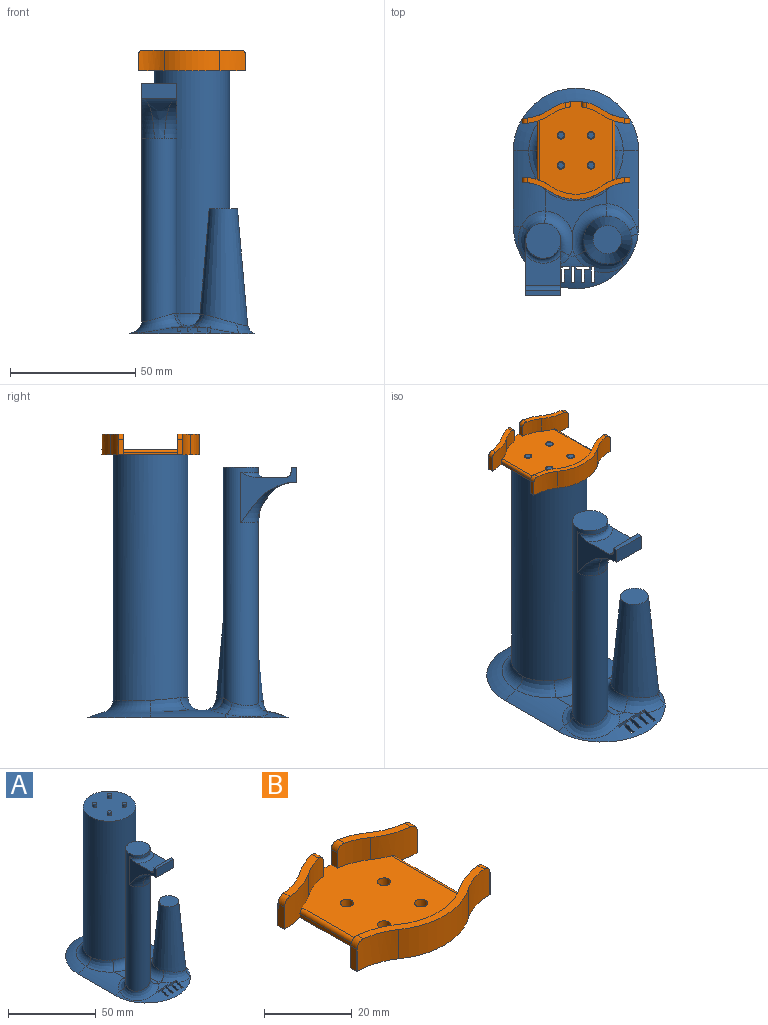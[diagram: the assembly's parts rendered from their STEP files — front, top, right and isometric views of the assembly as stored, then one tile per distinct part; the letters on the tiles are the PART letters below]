
ASSEMBLY  parts=2 mates=1
PART A: 71 faces, bbox 75.8x97.1x107.7 mm
  f0: plane 0.12x0.04mm, normal (0,0,-1), area 0mm2, adj f52,f53,f60
  f1: plane 14x14mm, normal (0,0,1), area 153.9mm2, adj f3
  f2: plane 14x2mm, normal (0,0,1), area 28mm2, adj f52,f53,f54,f56
  f3: cylinder r=7mm len=93.92mm, axis (0,0,-1), area 3634.1mm2, adj f1,f44,f45,f48,f52,f54,f58,f59
  f4: torus R=12.11mm, axis (0,0,-1), area 1.8mm2, adj f31,f38,f46
  f5: plane 24.21x16.62mm, normal (0,0,1), area 156mm2, adj f37,f38,f40,f48,f51
  f6: plane 2.56x2.06mm, normal (0,1,0), area 4.9mm2, adj f7,f29,f31,f39
  f7: plane 5.19x2.42mm, normal (-1,0,0), area 9.1mm2, adj f6,f8,f31,f39
  f8: plane 1.32x0.94mm, normal (0,1,0), area 1.1mm2, adj f7,f9,f31,f39
  f9: plane 5.19x2.34mm, normal (1,0,0), area 8.6mm2, adj f8,f10,f31,f39
  f10: plane 2.4x2.06mm, normal (0,1,0), area 4.5mm2, adj f9,f11,f31,f39
  f11: plane 2.39x1.01mm, normal (1,0,0), area 2.3mm2, adj f10,f12,f31,f39
  f12: plane 5.29x2.67mm, normal (0,-1,0), area 13.5mm2, adj f11,f29,f31,f39
  f13: plane 1.32x1.12mm, normal (0,1,0), area 1.4mm2, adj f14,f26,f31,f39
  f14: plane 6.19x2.68mm, normal (1,0,0), area 12.3mm2, adj f13,f15,f31,f39
  f15: plane 2.72x1.32mm, normal (0,-1,0), area 3.5mm2, adj f14,f26,f31,f39
  f16: plane 2.54x2.06mm, normal (0,1,0), area 4.9mm2, adj f17,f27,f31,f39
  f17: plane 5.19x2.48mm, normal (-1,0,0), area 9.5mm2, adj f16,f18,f31,f39
  f18: plane 1.32x1.08mm, normal (0,1,0), area 1.3mm2, adj f17,f19,f31,f39
  f19: plane 5.26x2.59mm, normal (1,0,0), area 9.7mm2, adj f18,f20,f31,f39
  f20: plane 2.6x2.06mm, normal (0,1,0), area 5.1mm2, adj f19,f21,f31,f39
  f21: plane 2.7x1mm, normal (1,0,0), area 2.6mm2, adj f20,f22,f31,f39
  f22: plane 5.34x2.74mm, normal (0,-1,0), area 14.1mm2, adj f21,f27,f31,f39,f50
  f23: plane 1.32x0.8mm, normal (0,1,0), area 0.9mm2, adj f24,f28,f31,f39
  f24: plane 6.23x2.71mm, normal (1,0,0), area 11mm2, adj f23,f25,f31,f39,f50
  f25: plane 2.78x1.32mm, normal (0,-1,0), area 3.5mm2, adj f24,f28,f31,f50
  f26: plane 6.22x2.73mm, normal (-1,0,0), area 12.5mm2, adj f13,f15,f31,f39
  f27: plane 2.66x1.02mm, normal (-1,0,0), area 2.5mm2, adj f16,f22,f31,f39,f50
  f28: plane 6.26x2.83mm, normal (-1,0,0), area 10.3mm2, adj f23,f25,f31,f39,f50
  f29: plane 2.67x1mm, normal (-1,0,0), area 2.6mm2, adj f6,f12,f31,f39
  f30: plane 3.1x2.31mm, normal (0,0,1), area 3.1mm2, adj f39,f48,f51
  f31: plane 80.03x50.03mm, normal (0,0,-1), area 3423.5mm2, adj f4,f6,f7,f8,f9,f10,f11,f12
  f32: cone r=10mm half-angle=5deg, axis (0,0,-1), area 2093.8mm2, adj f33,f46,f47,f49,f50,f51
  f33: plane 11.25x11.25mm, normal (0,0,1), area 99.4mm2, adj f32
  f34: cylinder r=15mm len=97.92mm, axis (0,0,-1), area 9198.3mm2, adj f35,f40,f41,f42,f43
  f35: plane 30x30mm, normal (0,0,1), area 687.2mm2, adj f34,f63,f65,f67,f69
  f36: torus R=12.11mm, axis (0,0,-1), area 452.2mm2, adj f31,f37,f38,f43
  f37: cylinder r=29.21mm len=30mm, axis (0,1,0), area 295.9mm2, adj f5,f31,f36,f39,f42,f45
  f38: cylinder r=29.21mm len=30mm, axis (0,1,0), area 247.3mm2, adj f4,f5,f31,f36,f41,f49
  f39: torus R=12.11mm, axis (0,0,-1), area 233.6mm2, adj f6,f7,f8,f9,f10,f11,f12,f13
  f40: torus R=20mm, axis (0,0,1), area 171.7mm2, adj f5,f34,f41,f42
  f41: bspline ~18.77x10.38mm, area 108.9mm2, adj f34,f38,f40,f43
  f42: bspline ~20.28x12.34mm, area 108.9mm2, adj f34,f37,f40,f43
  f43: torus R=20mm, axis (0,0,1), area 343.9mm2, adj f34,f36,f41,f42
  f44: bspline ~20.85x18.89mm, area 173mm2, adj f3,f39,f45,f48
  f45: bspline ~12.73x9.87mm, area 67.8mm2, adj f3,f37,f44,f48
  f46: bspline ~6.9x5.13mm, area 15mm2, adj f4,f32,f47,f49
  f47: bspline ~14.92x7.71mm, area 52mm2, adj f31,f32,f46,f50
  f48: torus R=12mm, axis (0,0,1), area 138.8mm2, adj f3,f5,f30,f44,f45,f51
  f49: bspline ~15.27x12.51mm, area 87.3mm2, adj f32,f38,f46,f51
  f50: bspline ~20.55x9.05mm, area 113.9mm2, adj f22,f24,f25,f27,f28,f32,f39,f47
  f51: torus R=14.32mm, axis (0,0,1), area 168.7mm2, adj f5,f30,f32,f48,f49,f50
  f52: plane 22.58x22.53mm, normal (-1,0,0), area 167.8mm2, adj f0,f2,f3,f53,f56,f57,f60,f61
  f53: plane 14.09x6.09mm, normal (0,-1,0), area 84mm2, adj f0,f2,f52,f54,f55,f59
  f54: plane 22.58x22.53mm, normal (1,0,0), area 167.8mm2, adj f2,f3,f53,f55,f56,f57,f58,f61
  f55: plane 0.12x0.04mm, normal (0,0,-1), area 0mm2, adj f53,f54,f58
  f56: plane 14x2mm, normal (0,1,0), area 28mm2, adj f2,f52,f54,f62
  f57: plane 14x12.34mm, normal (0,0,1), area 140.2mm2, adj f52,f54,f61,f62
  f58: torus R=23.05mm, axis (0,0,1), area 102.5mm2, adj f3,f54,f55,f59
  f59: bspline ~16.44x15.84mm, area 186.4mm2, adj f3,f53,f58,f60
  f60: torus R=23.05mm, axis (0,0,1), area 102.5mm2, adj f0,f3,f52,f59
  f61: torus R=9mm, axis (0,0,1), area 59mm2, adj f3,f52,f54,f57
  f62: cylinder r=2mm len=14mm, axis (1,0,0), area 44mm2, adj f52,f54,f56,f57
  f63: cylinder r=1.25mm len=2.5mm, axis (0,0,-1), area 15.7mm2, adj f35,f64
  f64: plane 2.5x2.5mm, normal (0,0,1), area 4.9mm2, adj f63
  f65: cylinder r=1.25mm len=2.5mm, axis (0,0,-1), area 15.7mm2, adj f35,f66
  f66: plane 2.5x2.5mm, normal (0,0,1), area 4.9mm2, adj f65
  f67: cylinder r=1.25mm len=2.5mm, axis (0,0,-1), area 15.7mm2, adj f35,f68
  f68: plane 2.5x2.5mm, normal (0,0,1), area 4.9mm2, adj f67
  f69: cylinder r=1.25mm len=2.5mm, axis (0,0,-1), area 15.7mm2, adj f35,f70
  f70: plane 2.5x2.5mm, normal (0,0,1), area 4.9mm2, adj f69
PART B: 46 faces, bbox 43x39x8.2 mm
  f0: plane 15.25x8.18mm, normal (0,0,1), area 33.2mm2, adj f2,f4,f5,f9,f39,f42
  f1: cylinder r=17.5mm len=7.77mm, axis (0,0,-1), area 51.3mm2, adj f3,f14,f35,f37,f38
  f2: cylinder r=19.5mm len=22.32mm, axis (0,0,-1), area 165.2mm2, adj f0,f9,f10,f14,f15,f35,f36,f37
  f3: cylinder r=20mm len=11.45mm, axis (0,0,-1), area 87.1mm2, adj f1,f13,f14,f15,f30,f35,f43,f44
  f4: cylinder r=17.5mm len=7.77mm, axis (0,0,-1), area 51.3mm2, adj f0,f5,f35,f36,f39
  f5: cylinder r=20mm len=11.45mm, axis (0,0,-1), area 87.1mm2, adj f0,f4,f6,f15,f29,f35,f42,f45
  f6: plane 6.58x0.04mm, normal (0,-1,0), area 0.2mm2, adj f5,f7,f15,f42
  f7: plane 6.2x2mm, normal (1,0,0), area 12.4mm2, adj f6,f8,f15,f42
  f8: plane 6.58x0.04mm, normal (0,1,0), area 0.2mm2, adj f7,f9,f15,f42
  f9: cylinder r=18mm len=10.3mm, axis (0,0,-1), area 89.1mm2, adj f0,f2,f8,f15,f42
  f10: cylinder r=18mm len=10.3mm, axis (0,0,-1), area 89.1mm2, adj f2,f11,f14,f15,f43
  f11: plane 6.58x0.04mm, normal (0,1,0), area 0.2mm2, adj f10,f12,f15,f43
  f12: plane 6.2x2mm, normal (-1,0,0), area 12.4mm2, adj f11,f13,f15,f43
  f13: plane 6.58x0.04mm, normal (0,-1,0), area 0.2mm2, adj f3,f12,f15,f43
  f14: plane 15.25x8.18mm, normal (0,0,1), area 33.2mm2, adj f1,f2,f3,f10,f38,f43
  f15: plane 43x39mm, normal (0,0,-1), area 1097mm2, adj f2,f3,f5,f6,f7,f8,f9,f10
  f16: cylinder r=20mm len=11.45mm, axis (0,0,-1), area 87.1mm2, adj f15,f17,f27,f28,f30,f35,f41,f44
  f17: plane 6.58x0.04mm, normal (0,1,0), area 0.2mm2, adj f15,f16,f18,f41
  f18: plane 6.2x2mm, normal (-1,0,0), area 12.4mm2, adj f15,f17,f19,f41
  f19: plane 6.58x0.04mm, normal (0,-1,0), area 0.2mm2, adj f15,f18,f20,f41
  f20: cylinder r=18mm len=10.3mm, axis (0,0,-1), area 89.1mm2, adj f15,f19,f21,f28,f41
  f21: cylinder r=19.5mm len=22.32mm, axis (0,0,-1), area 194.9mm2, adj f15,f20,f22,f28
  f22: cylinder r=18mm len=10.3mm, axis (0,0,-1), area 89.1mm2, adj f15,f21,f23,f28,f40
  f23: plane 6.58x0.04mm, normal (0,-1,0), area 0.2mm2, adj f15,f22,f24,f40
  f24: plane 6.2x2mm, normal (1,0,0), area 12.4mm2, adj f15,f23,f25,f40
  f25: plane 6.58x0.04mm, normal (0,1,0), area 0.2mm2, adj f15,f24,f26,f40
  f26: cylinder r=20mm len=11.45mm, axis (0,0,-1), area 87.1mm2, adj f15,f25,f27,f28,f29,f35,f40,f45
  f27: cylinder r=17.5mm len=20.03mm, axis (0,0,-1), area 132.2mm2, adj f16,f26,f28,f35
  f28: plane 39x8.65mm, normal (0,0,1), area 83.5mm2, adj f16,f20,f21,f22,f26,f27,f40,f41
  f29: plane 23.32x1mm, normal (1,0,0), area 23.3mm2, adj f5,f15,f26,f45
  f30: plane 23.32x1mm, normal (-1,0,0), area 23.3mm2, adj f3,f15,f16,f44
  f31: cylinder r=1.5mm len=3mm, axis (0,0,-1), area 18.8mm2, adj f15,f35
  f32: cylinder r=1.5mm len=3mm, axis (0,0,-1), area 18.8mm2, adj f15,f35
  f33: cylinder r=1.5mm len=3mm, axis (0,0,-1), area 18.8mm2, adj f15,f35
  f34: cylinder r=1.5mm len=3mm, axis (0,0,-1), area 18.8mm2, adj f15,f35
  f35: plane 37x29mm, normal (0,0,1), area 875.6mm2, adj f1,f2,f3,f4,f5,f16,f26,f27
  f36: plane 4.2x2.02mm, normal (-1,0,0), area 8.5mm2, adj f2,f4,f35,f39
  f37: plane 4.2x2.02mm, normal (1,0,0), area 8.5mm2, adj f1,f2,f35,f38
  f38: cylinder r=2mm len=2.39mm, axis (0,1,0), area 6.4mm2, adj f1,f2,f14,f37
  f39: cylinder r=2mm len=2.39mm, axis (0,-1,0), area 6.4mm2, adj f0,f2,f4,f36
  f40: cylinder r=2mm len=2.11mm, axis (0,-1,0), area 6.3mm2, adj f22,f23,f24,f25,f26,f28
  f41: cylinder r=2mm len=2.11mm, axis (0,1,0), area 6.3mm2, adj f16,f17,f18,f19,f20,f28
  f42: cylinder r=2mm len=2.11mm, axis (0,-1,0), area 6.3mm2, adj f0,f5,f6,f7,f8,f9
  f43: cylinder r=2mm len=2.11mm, axis (0,1,0), area 6.3mm2, adj f3,f10,f11,f12,f13,f14
  f44: cylinder r=1mm len=24mm, axis (0,1,0), area 37mm2, adj f3,f16,f30,f35
  f45: cylinder r=1mm len=24mm, axis (0,-1,0), area 37mm2, adj f5,f26,f29,f35
PLACE A t=(-9.87,16.69,-18.54)mm
PLACE B t=(-9.87,31.69,86.46)mm
MATE fastened B.f21 <-> A.f34  axis (0,0,-1) through (-9.87,31.69,86.46)mm
